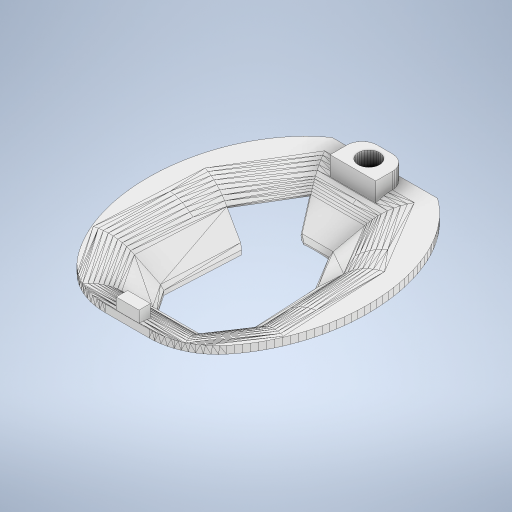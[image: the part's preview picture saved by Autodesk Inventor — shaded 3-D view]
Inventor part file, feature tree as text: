
AUTODESK INVENTOR PART (.ipt)
format: ipt  version: 2023.5 (Build 275446000, 446)  size: 1,233,920 bytes
history: native  units: in
note: dims shown in document units (in); Inventor stores cm internally (conversion verified against a paired STEP export)
features: other x3, extrude x3, sketch x3, direct_edit x1
ambient origin geometry x8: Origin, YZ Plane, XZ Plane, XY Plane, X Axis, Y Axis, Z Axis, Center Point
bodies: Solid1 (feature_tree)
feature tree (10):
  other  "rat_cap_base_v8"
  other  "MeshFeature1"
  extrude  "Extrusion1"  TaperAngle=0.0deg  [1 undecoded]
  extrude  "Extrusion2"  Depth=0.0155in
  extrude  "Extrusion3"  [1 undecoded]
  direct_edit  "Direct Edit1"
  sketch  "Sketch1"  dims[d0=0.0in d1=0.0in d2=0.0in d3=0.0in]
  sketch  "Sketch2"  dims[d4=0.0in d5=0.0in d6=0.0155in d7=0.3937in d8=0.3937in]
  sketch  "Sketch3"
  other  "Scale1"
note: 2 required parameter values undecoded (feature->parameter linkage not recoverable at this tier; creation-order binding heuristic only, values carry confidence <= 0.55)
